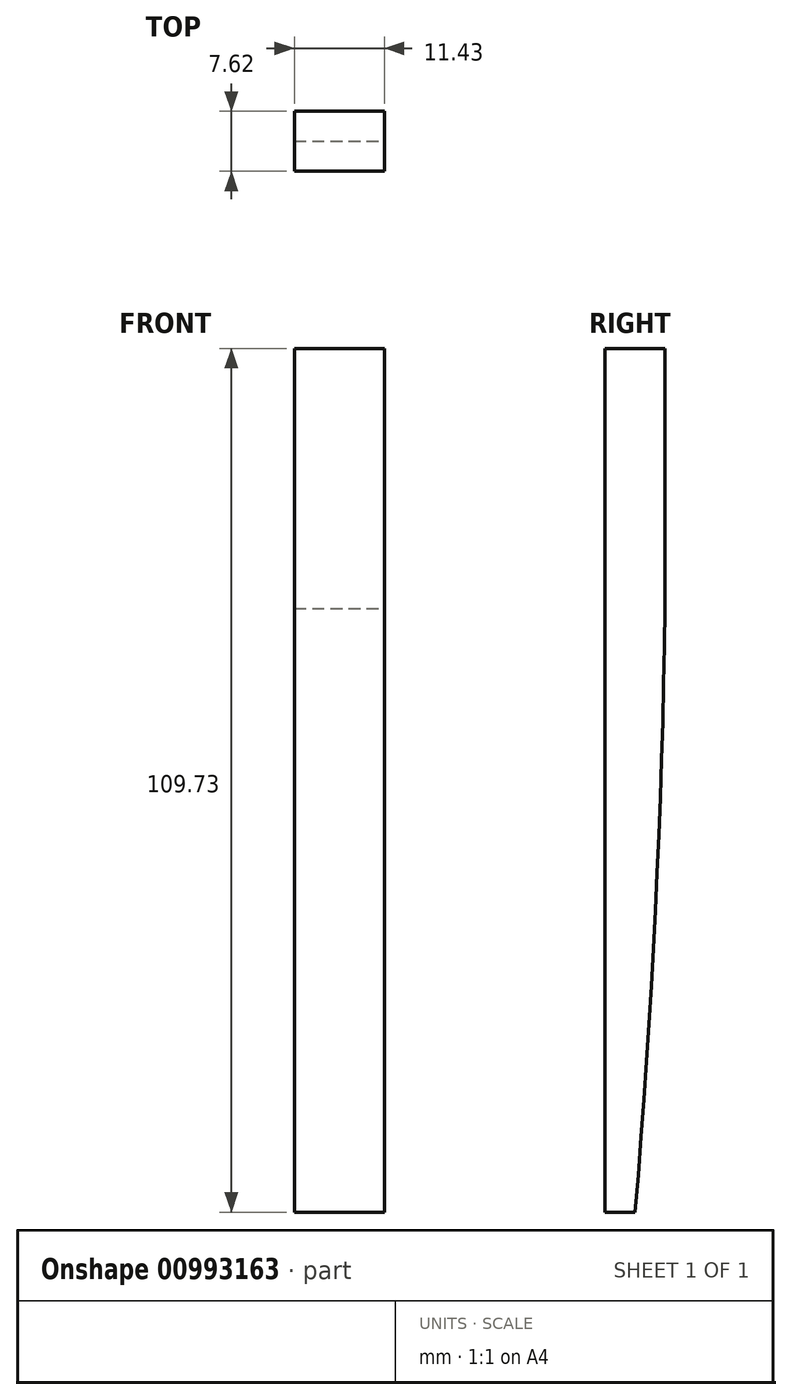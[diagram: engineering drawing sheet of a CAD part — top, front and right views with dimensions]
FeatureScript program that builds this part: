
annotation { "Feature Type Name" : "Feature", "Feature Type Description" : "" }
export const myFeature = defineFeature(function(context is Context, id is Id, definition is map)
    precondition{}
    {
        {
            var Q0;
            Q0=qCreatedBy(makeId("Front.planeOp"),FACE);
            var sketch = newSketch(context, id + "F0", { "sketchPlane" : qUnion([Q0])});
            skLineSegment(sketch, "E0.bottom", {"start": v(47.17, 65.39) * mm, "end": v(35.74, 65.39) * mm});
            skLineSegment(sketch, "E0.top", {"start": v(47.17, -44.34) * mm, "end": v(35.74, -44.34) * mm});
            skLineSegment(sketch, "E0.left", {"start": v(47.17, 65.39) * mm, "end": v(47.17, -44.34) * mm});
            skLineSegment(sketch, "E0.right", {"start": v(35.74, 65.39) * mm, "end": v(35.74, -44.34) * mm});
            skSolve(sketch);
        }
        {
            var Q0;
            Q0=makeQuery(id+"F0.imprint","IMPRINT",FACE,{"disambiguationData":[TD([[makeQuery(id+"F0.imprint","IMPRINT",EDGE,{"derivedFrom":sQuery(id+"F0.wireOp",EDGE,"E0.bottom")}),1.0]])]});
            extrude(context, id + "F1", {"entities" : qUnion([Q0]), "depth" : 7.62 * mm, "offsetDistance" : 25.4 * mm});
        }
        {
            var Q0;
            Q0=makeQuery(id+"F1.opExtrude","SWEPT_FACE",FACE,{"disambiguationData":[OSD([sQuery(id+"F0.wireOp",EDGE,"E0.left")])]});
            var sketch = newSketch(context, id + "F2", { "sketchPlane" : qUnion([Q0])});
            skArc(sketch, "E1", {"start": v(-3.81, -44.34) * mm, "mid": v(-0.54, 10.47) * mm, "end": v(0, 65.39) * mm});
            skSolve(sketch);
        }
        {
            var Q0;
            {var subQ0=sQuery(id+"F2.wireOp",EDGE,"E1");var subQ1=sQuery(id+"F0.wireOp",EDGE,"E0.left");var subQ4=makeQuery(id+"F1.opExtrude","CAP_EDGE",EDGE,{"disambiguationData":[OSD([subQ1])],"isStart":true});var subQ5=makeQuery(id+"F2.imprint","INTERSECT",VERTEX,{"derivedFrom":[subQ4,subQ0]});Q0=makeQuery(id+"F2.imprint","IMPRINT",FACE,{"disambiguationData":[TD([[makeQuery(id+"F2.imprint","IMPRINT",EDGE,{"disambiguationData":[TD([[subQ5,1.0]])],"derivedFrom":subQ0}),-1.0]])]});}
            extrude(context, id + "F3", {"entities" : qUnion([Q0]), "operationType" : NewBodyOperationType.REMOVE, "oppositeDirection" : true, "depth" : 25.4 * mm, "offsetDistance" : 25.4 * mm});
        }
    });
